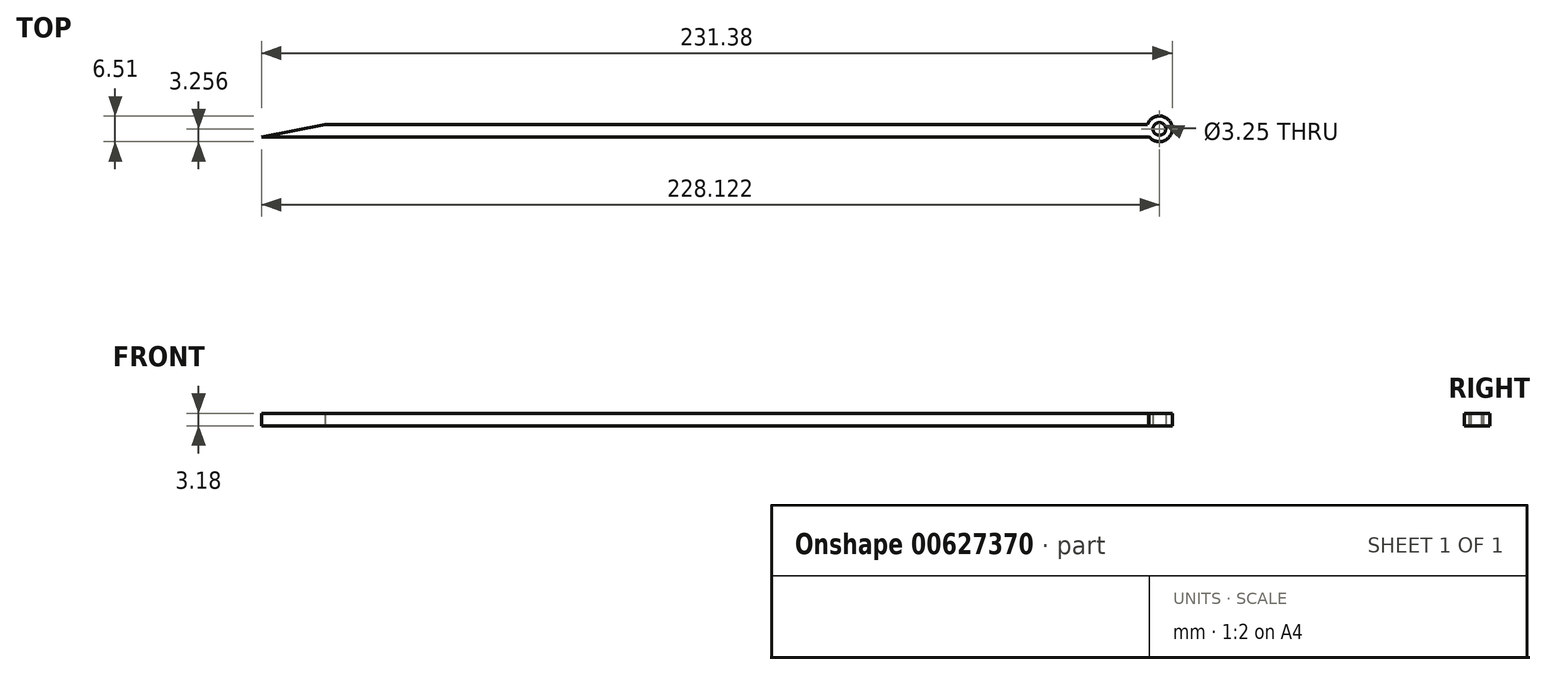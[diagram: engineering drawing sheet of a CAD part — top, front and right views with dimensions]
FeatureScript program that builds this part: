
annotation { "Feature Type Name" : "Feature", "Feature Type Description" : "" }
export const myFeature = defineFeature(function(context is Context, id is Id, definition is map)
    precondition{}
    {
        {
            var Q0;
            Q0=qCreatedBy(makeId("Top.planeOp"),FACE);
            var sketch = newSketch(context, id + "F0", { "sketchPlane" : qUnion([Q0])});
            skLineSegment(sketch, "E0", {"start": v(-92.47, 10.1) * mm, "end": v(116.86, 10.1) * mm});
            skLineSegment(sketch, "E1", {"start": v(116.86, 10.1) * mm, "end": v(116.86, 6.92) * mm});
            skLineSegment(sketch, "E2", {"start": v(116.86, 6.92) * mm, "end": v(-108.64, 6.92) * mm});
            skLineSegment(sketch, "E3", {"start": v(-108.64, 6.92) * mm, "end": v(-92.47, 10.1) * mm});
            skCircle(sketch, "E4", {"center": v(121.24, 9.33) * mm, "radius": 3.01 * mm});
            skSolve(sketch);
        }
        {
            var Q0;
            Q0=makeQuery(id+"F0.imprint","IMPRINT",FACE,{"disambiguationData":[TD([[makeQuery(id+"F0.imprint","IMPRINT",EDGE,{"derivedFrom":sQuery(id+"F0.wireOp",EDGE,"E0")}),-1.0]])]});
            extrude(context, id + "F1", {"entities" : qUnion([Q0]), "depth" : 3.17 * mm, "offsetDistance" : 25.4 * mm});
        }
        {
            var Q0;
            Q0=qCreatedBy(makeId("Top.planeOp"),FACE);
            var sketch = newSketch(context, id + "F2", { "sketchPlane" : qUnion([Q0])});
            skCircle(sketch, "E5", {"center": v(119.48, 8.96) * mm, "radius": 3.26 * mm});
            skCircle(sketch, "E6", {"center": v(119.48, 8.96) * mm, "radius": 1.62 * mm});
            skSolve(sketch);
        }
        {
            var Q0;
            Q0=makeQuery(id+"F2.imprint","IMPRINT",FACE,{"disambiguationData":[TD([[makeQuery(id+"F2.imprint","IMPRINT",EDGE,{"derivedFrom":sQuery(id+"F2.wireOp",EDGE,"E5")}),1.0]])]});
            extrude(context, id + "F3", {"entities" : qUnion([Q0]), "operationType" : NewBodyOperationType.ADD, "depth" : 3.17 * mm, "offsetDistance" : 25.4 * mm});
        }
    });
